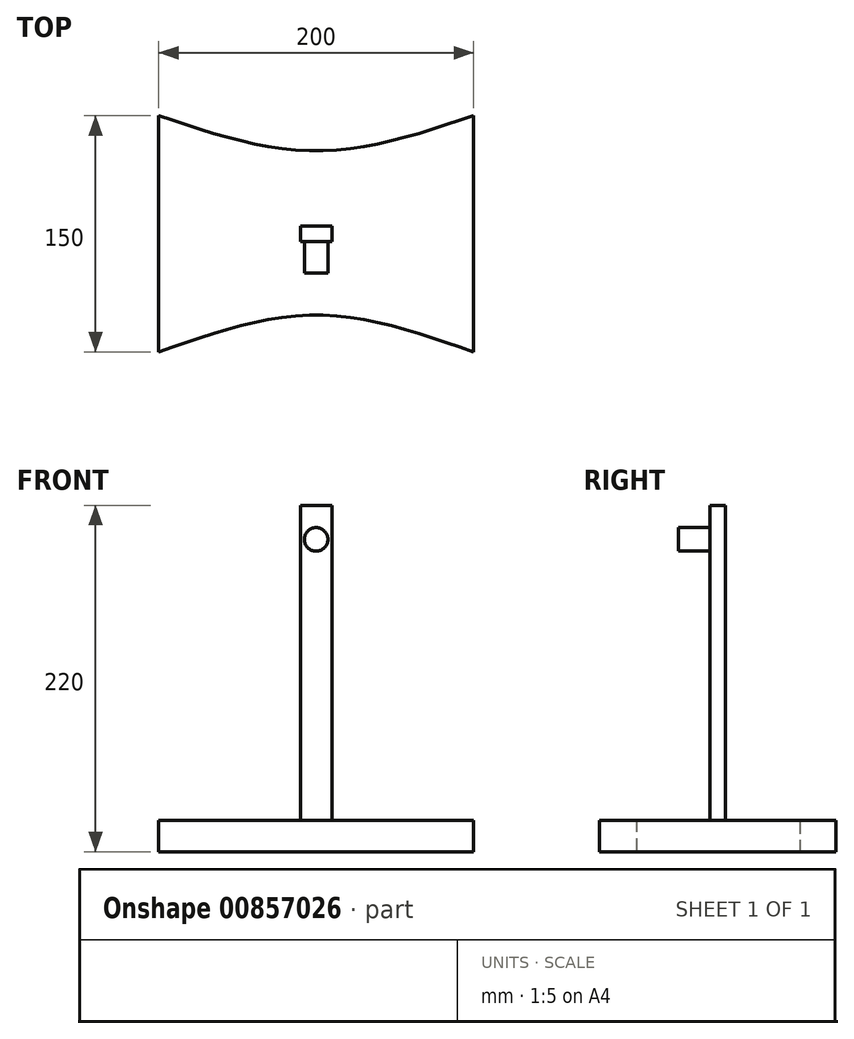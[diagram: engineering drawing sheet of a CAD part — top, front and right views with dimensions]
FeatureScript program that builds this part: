
annotation { "Feature Type Name" : "Feature", "Feature Type Description" : "" }
export const myFeature = defineFeature(function(context is Context, id is Id, definition is map)
    precondition{}
    {
        {
            var Q0;
            Q0=qCreatedBy(makeId("Top.planeOp"),FACE);
            var sketch = newSketch(context, id + "F0", { "sketchPlane" : qUnion([Q0])});
            skLineSegment(sketch, "E0.left", {"start": v(100, -75) * mm, "end": v(100, 75) * mm});
            skLineSegment(sketch, "E0.right", {"start": v(-100, -75) * mm, "end": v(-100, 75) * mm});
            skPoint(sketch, "E0.middle", {"position": v(0, 0) * mm});
            skFitSpline(sketch, "E1", {"points": [v(-100, 75) * mm, v(0, 52.68) * mm, v(100, 75) * mm], "startDerivative": vector(200, -66.96) * mm, "endDerivative": vector(200, 66.96) * mm});
            skFitSpline(sketch, "E2", {"points": [v(-100, -75) * mm, v(0, -51.56) * mm, v(100, -75) * mm], "startDerivative": vector(200, 70.32) * mm, "endDerivative": vector(200, -70.32) * mm});
            skSolve(sketch);
        }
        {
            var Q0;
            Q0=makeQuery(id+"F0.imprint","IMPRINT",FACE,{"disambiguationData":[TD([[makeQuery(id+"F0.imprint","IMPRINT",EDGE,{"derivedFrom":sQuery(id+"F0.wireOp",EDGE,"E0.left")}),1.0]])]});
            extrude(context, id + "F1", {"entities" : qUnion([Q0]), "depth" : 20 * mm, "offsetDistance" : 25 * mm});
        }
        {
            var Q0;
            Q0=makeQuery(id+"F1.opExtrude","CAP_FACE",FACE,{"disambiguationData":[OSD([sQuery(id+"F0.wireOp",EDGE,"E0.left"),sQuery(id+"F0.wireOp",EDGE,"E0.right"),sQuery(id+"F0.wireOp",EDGE,"E1"),sQuery(id+"F0.wireOp",EDGE,"E2")])],"isStart":false});
            var sketch = newSketch(context, id + "F2", { "sketchPlane" : qUnion([Q0])});
            skLineSegment(sketch, "E3.bottom", {"start": v(10, -5) * mm, "end": v(-10, -5) * mm});
            skLineSegment(sketch, "E3.top", {"start": v(10, 5) * mm, "end": v(-10, 5) * mm});
            skLineSegment(sketch, "E3.left", {"start": v(10, -5) * mm, "end": v(10, 5) * mm});
            skLineSegment(sketch, "E3.right", {"start": v(-10, -5) * mm, "end": v(-10, 5) * mm});
            skPoint(sketch, "E3.middle", {"position": v(0, 0) * mm});
            skSolve(sketch);
        }
        {
            var Q0;
            Q0=makeQuery(id+"F2.imprint","IMPRINT",FACE,{"disambiguationData":[TD([[makeQuery(id+"F2.imprint","IMPRINT",EDGE,{"derivedFrom":sQuery(id+"F2.wireOp",EDGE,"E3.bottom")}),-1.0]])]});
            extrude(context, id + "F3", {"entities" : qUnion([Q0]), "operationType" : NewBodyOperationType.ADD, "depth" : 200 * mm, "offsetDistance" : 25 * mm});
        }
        {
            var Q0;
            Q0=makeQuery(id+"F3.opExtrude","SWEPT_FACE",FACE,{"disambiguationData":[OSD([sQuery(id+"F2.wireOp",EDGE,"E3.bottom")])]});
            var sketch = newSketch(context, id + "F4", { "sketchPlane" : qUnion([Q0])});
            skCircle(sketch, "E4", {"center": v(0, 198.4) * mm, "radius": 7.5 * mm});
            skPoint(sketch, "E4.centerSnap0", {"position": v(0, 220) * mm});
            skSolve(sketch);
        }
        {
            var Q0;
            Q0=makeQuery(id+"F4.imprint","IMPRINT",FACE,{"disambiguationData":[TD([[makeQuery(id+"F4.imprint","IMPRINT",EDGE,{"derivedFrom":sQuery(id+"F4.wireOp",EDGE,"E4")}),1.0]])]});
            extrude(context, id + "F5", {"entities" : qUnion([Q0]), "depth" : 20 * mm, "offsetDistance" : 25 * mm});
        }
    });
